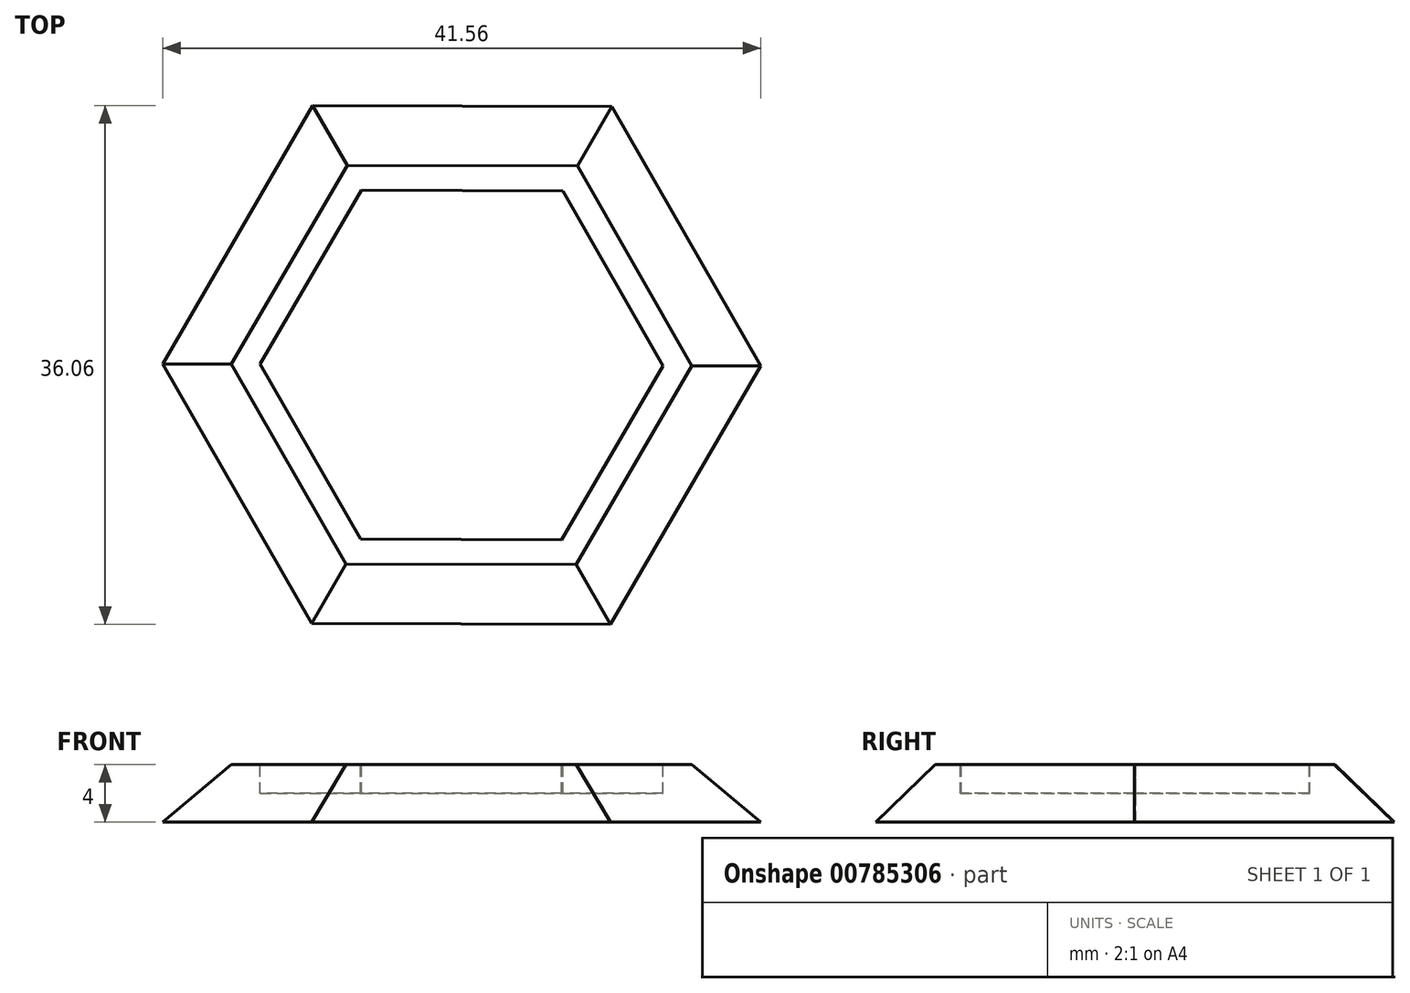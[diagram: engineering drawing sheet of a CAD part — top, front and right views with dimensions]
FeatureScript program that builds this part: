
annotation { "Feature Type Name" : "Feature", "Feature Type Description" : "" }
export const myFeature = defineFeature(function(context is Context, id is Id, definition is map)
    precondition{}
    {
        {
            var Q0;
            Q0=qCreatedBy(makeId("Top.planeOp"),FACE);
            var sketch = newSketch(context, id + "F0", { "sketchPlane" : qUnion([Q0])});
            skCircle(sketch, "E0.cCircle", {"center": v(0, 0) * mm, "radius": 18 * mm, "construction": true});
            skLineSegment(sketch, "E0.0", {"start": v(10.44, 17.97) * mm, "end": v(20.78, -0.05) * mm});
            skLineSegment(sketch, "E0.1", {"start": v(20.78, -0.05) * mm, "end": v(10.35, -18.03) * mm});
            skLineSegment(sketch, "E0.2", {"start": v(10.35, -18.03) * mm, "end": v(-10.44, -17.97) * mm});
            skLineSegment(sketch, "E0.3", {"start": v(-10.44, -17.97) * mm, "end": v(-20.78, 0.05) * mm});
            skLineSegment(sketch, "E0.4", {"start": v(-20.78, 0.05) * mm, "end": v(-10.35, 18.03) * mm});
            skLineSegment(sketch, "E0.5", {"start": v(-10.35, 18.03) * mm, "end": v(10.44, 17.97) * mm});
            skPoint(sketch, "E0.0.midPoint", {"position": v(15.61, 8.96) * mm});
            skSolve(sketch);
        }
        {
            var Q0;
            Q0=qCreatedBy(makeId("Top.planeOp"),FACE);
            cPlane(context, id + "F1", {"entities" : qUnion([Q0]), "cplaneType" : CPlaneType.OFFSET, "offset" : 4 * mm, "width" : 150 * mm, "height" : 150 * mm});
        }
        {
            var Q0;
            Q0=qCreatedBy(id+"F1.planeOp",FACE);
            var sketch = newSketch(context, id + "F2", { "sketchPlane" : qUnion([Q0])});
            skCircle(sketch, "E1.cCircle", {"center": v(0, 0) * mm, "radius": 13.86 * mm, "construction": true});
            skLineSegment(sketch, "E1.0", {"start": v(16, -0.05) * mm, "end": v(7.96, -13.88) * mm});
            skLineSegment(sketch, "E1.1", {"start": v(7.96, -13.88) * mm, "end": v(-8.04, -13.83) * mm});
            skLineSegment(sketch, "E1.2", {"start": v(-8.04, -13.83) * mm, "end": v(-16, 0.05) * mm});
            skLineSegment(sketch, "E1.3", {"start": v(-16, 0.05) * mm, "end": v(-7.96, 13.88) * mm});
            skLineSegment(sketch, "E1.4", {"start": v(-7.96, 13.88) * mm, "end": v(8.04, 13.83) * mm});
            skLineSegment(sketch, "E1.5", {"start": v(8.04, 13.83) * mm, "end": v(16, -0.05) * mm});
            skPoint(sketch, "E1.0.midPoint", {"position": v(11.98, -6.97) * mm});
            skLineSegment(sketch, "E2", {"start": v(16, -0.05) * mm, "end": v(20.78, -0.05) * mm});
            skLineSegment(sketch, "E3", {"start": v(-16, 0.05) * mm, "end": v(-20.78, 0.05) * mm});
            skPoint(sketch, "E4.1.5.end.orphan", {"position": v(10.44, 17.97) * mm});
            skPoint(sketch, "E4.1.3.end.orphan", {"position": v(10.35, -18.03) * mm});
            skPoint(sketch, "E4.1.2.end.orphan", {"position": v(-10.44, -17.97) * mm});
            skPoint(sketch, "E4.0.end.orphan", {"position": v(-10.44, -17.97) * mm});
            skPoint(sketch, "E4.0.start.orphan", {"position": v(10.35, -18.03) * mm});
            skPoint(sketch, "E4.1.1.start.orphan", {"position": v(-10.35, 18.03) * mm});
            skSolve(sketch);
        }
        {
            var Q0;
            Q0 = qSketchRegion(id + "F0", true);
            var Q1;
            Q1 = qSketchRegion(id + "F2", true);
            loft(context, id + "F3", {"sheetProfilesArray" : [{ "sheetProfileEntities" : qUnion([Q0]) }, { "sheetProfileEntities" : qUnion([Q1]) }]});
        }
        {
            var Q0;
            Q0=makeQuery(id+"F3.opLoft","CAP_FACE",FACE,{"disambiguationData":[OSD([makeQuery(id+"F2.imprint","IMPRINT",FACE,{"disambiguationData":[TD([[makeQuery(id+"F2.imprint","IMPRINT",EDGE,{"derivedFrom":sQuery(id+"F2.wireOp",EDGE,"E1.0")}),-1.0]])]})])],"isStart":true});
            var sketch = newSketch(context, id + "F4", { "sketchPlane" : qUnion([Q0])});
            skCircle(sketch, "E5.cCircle", {"center": v(0, 0) * mm, "radius": 12.12 * mm, "construction": true});
            skLineSegment(sketch, "E5.0", {"start": v(14, -0.05) * mm, "end": v(6.96, -12.15) * mm});
            skLineSegment(sketch, "E5.1", {"start": v(6.96, -12.15) * mm, "end": v(-7.04, -12.1) * mm});
            skLineSegment(sketch, "E5.2", {"start": v(-7.04, -12.1) * mm, "end": v(-14, 0.05) * mm});
            skLineSegment(sketch, "E5.3", {"start": v(-14, 0.05) * mm, "end": v(-6.96, 12.15) * mm});
            skLineSegment(sketch, "E5.4", {"start": v(-6.96, 12.15) * mm, "end": v(7.04, 12.1) * mm});
            skLineSegment(sketch, "E5.5", {"start": v(7.04, 12.1) * mm, "end": v(14, -0.05) * mm});
            skPoint(sketch, "E5.0.midPoint", {"position": v(10.48, -6.1) * mm});
            skLineSegment(sketch, "E6", {"start": v(-16, 0.05) * mm, "end": v(-14, 0.05) * mm});
            skLineSegment(sketch, "E7", {"start": v(14, -0.05) * mm, "end": v(16, -0.05) * mm});
            skSolve(sketch);
        }
        {
            var Q0;
            Q0 = qSketchRegion(id + "F4", true);
            extrude(context, id + "F5", {"entities" : qUnion([Q0]), "operationType" : NewBodyOperationType.REMOVE, "oppositeDirection" : true, "depth" : 2 * mm, "offsetDistance" : 25 * mm});
        }
    });
